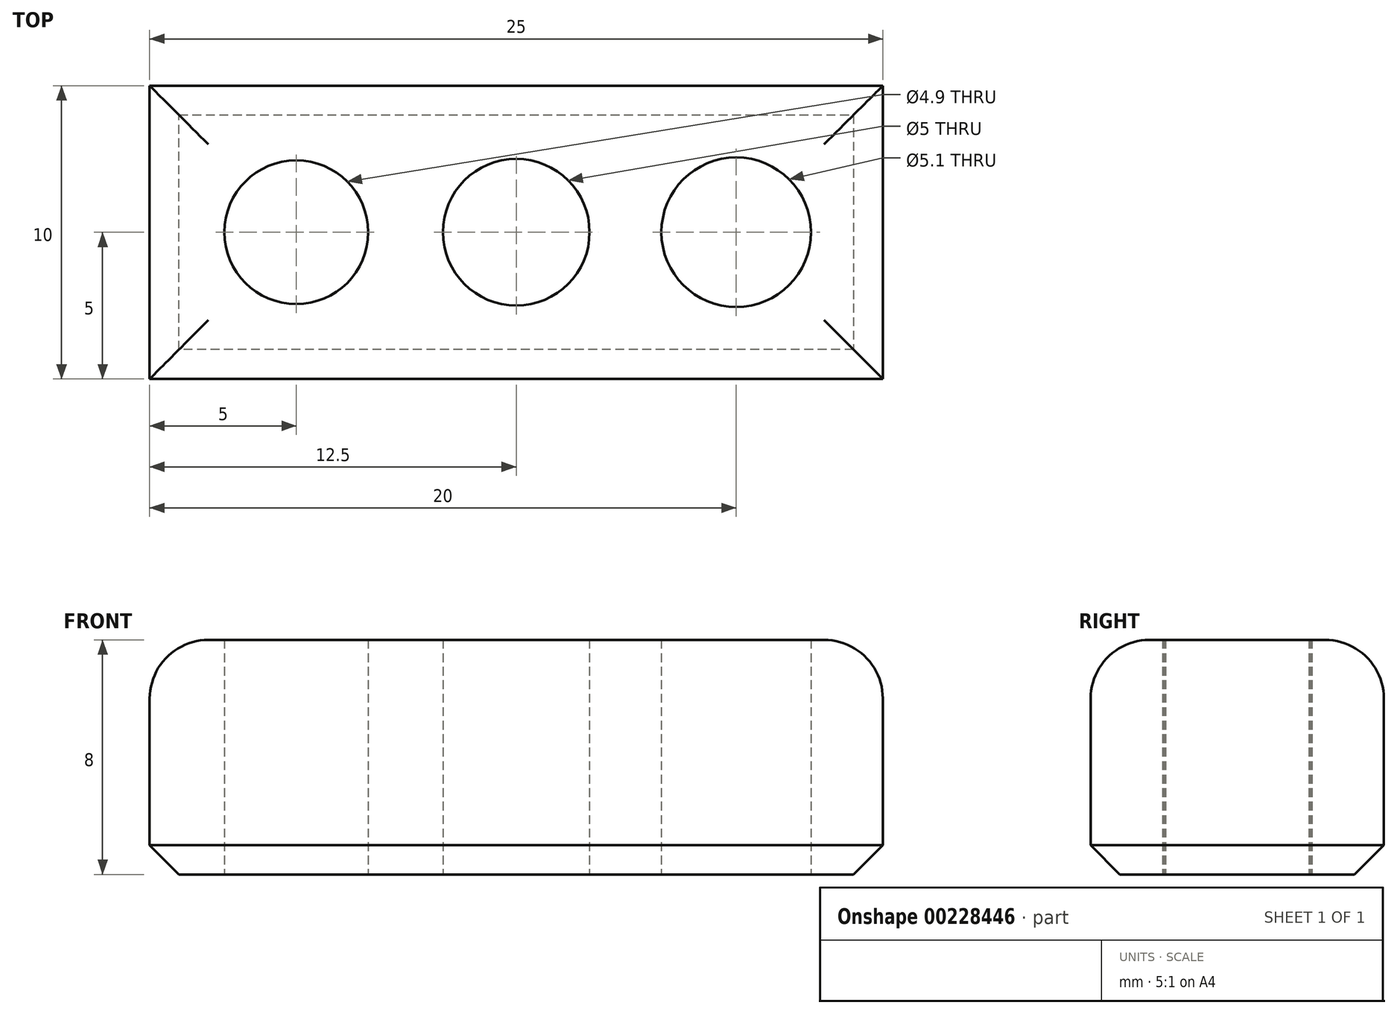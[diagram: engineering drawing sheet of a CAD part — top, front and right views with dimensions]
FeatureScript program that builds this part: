
annotation { "Feature Type Name" : "Feature", "Feature Type Description" : "" }
export const myFeature = defineFeature(function(context is Context, id is Id, definition is map)
    precondition{}
    {
        {
            var Q0;
            Q0=qCreatedBy(makeId("Top.planeOp"),FACE);
            var sketch = newSketch(context, id + "F0", { "sketchPlane" : qUnion([Q0])});
            skLineSegment(sketch, "E0.bottom", {"start": v(-12.5, 5) * mm, "end": v(12.5, 5) * mm});
            skLineSegment(sketch, "E0.top", {"start": v(-12.5, -5) * mm, "end": v(12.5, -5) * mm});
            skLineSegment(sketch, "E0.left", {"start": v(-12.5, 5) * mm, "end": v(-12.5, -5) * mm});
            skLineSegment(sketch, "E0.right", {"start": v(12.5, 5) * mm, "end": v(12.5, -5) * mm});
            skPoint(sketch, "E0.middle", {"position": v(0, 0) * mm});
            skLineSegment(sketch, "E1", {"start": v(-12.5, 0) * mm, "end": v(12.5, 0) * mm, "construction": true});
            skLineSegment(sketch, "E2", {"start": v(0, 5) * mm, "end": v(0, -5) * mm, "construction": true});
            skLineSegment(sketch, "E3", {"start": v(-7.5, 5) * mm, "end": v(-7.5, -5) * mm, "construction": true});
            skLineSegment(sketch, "E4", {"start": v(7.5, 5) * mm, "end": v(7.5, -5) * mm, "construction": true});
            skCircle(sketch, "E5", {"center": v(-7.5, 0) * mm, "radius": 2.45 * mm});
            skCircle(sketch, "E6", {"center": v(0, 0) * mm, "radius": 2.5 * mm});
            skCircle(sketch, "E7", {"center": v(7.5, 0) * mm, "radius": 2.55 * mm});
            skSolve(sketch);
        }
        {
            var Q0;
            Q0=makeQuery(id+"F0.imprint","IMPRINT",FACE,{"disambiguationData":[TD([[makeQuery(id+"F0.imprint","IMPRINT",EDGE,{"derivedFrom":sQuery(id+"F0.wireOp",EDGE,"E0.bottom")}),-1.0]])]});
            extrude(context, id + "F1", {"entities" : qUnion([Q0]), "depth" : 8 * mm});
        }
        {
            var Q0;
            Q0=makeQuery(id+"F1.opExtrude","CAP_EDGE",EDGE,{"disambiguationData":[OSD([sQuery(id+"F0.wireOp",EDGE,"E0.top")])],"isStart":false});
            var Q1;
            Q1=makeQuery(id+"F1.opExtrude","CAP_EDGE",EDGE,{"disambiguationData":[OSD([sQuery(id+"F0.wireOp",EDGE,"E0.left")])],"isStart":false});
            var Q2;
            Q2=makeQuery(id+"F1.opExtrude","CAP_EDGE",EDGE,{"disambiguationData":[OSD([sQuery(id+"F0.wireOp",EDGE,"E0.bottom")])],"isStart":false});
            var Q3;
            Q3=makeQuery(id+"F1.opExtrude","CAP_EDGE",EDGE,{"disambiguationData":[OSD([sQuery(id+"F0.wireOp",EDGE,"E0.right")])],"isStart":false});
            fillet(context, id + "F2", {"entities" : qUnion([Q0, Q1, Q2, Q3]), "radius" : 2 * mm, "tangentPropagation" : true, "allowEdgeOverflow" : false});
        }
        {
            var Q0;
            Q0=makeQuery(id+"F1.opExtrude","CAP_EDGE",EDGE,{"disambiguationData":[OSD([sQuery(id+"F0.wireOp",EDGE,"E0.left")])],"isStart":true});
            var Q1;
            Q1=makeQuery(id+"F1.opExtrude","CAP_EDGE",EDGE,{"disambiguationData":[OSD([sQuery(id+"F0.wireOp",EDGE,"E0.top")])],"isStart":true});
            var Q2;
            Q2=makeQuery(id+"F1.opExtrude","CAP_EDGE",EDGE,{"disambiguationData":[OSD([sQuery(id+"F0.wireOp",EDGE,"E0.bottom")])],"isStart":true});
            var Q3;
            Q3=makeQuery(id+"F1.opExtrude","CAP_EDGE",EDGE,{"disambiguationData":[OSD([sQuery(id+"F0.wireOp",EDGE,"E0.right")])],"isStart":true});
            chamfer(context, id + "F3", {"entities" : qUnion([Q0, Q1, Q2, Q3]), "width" : 1 * mm, "tangentPropagation" : true});
        }
    });
